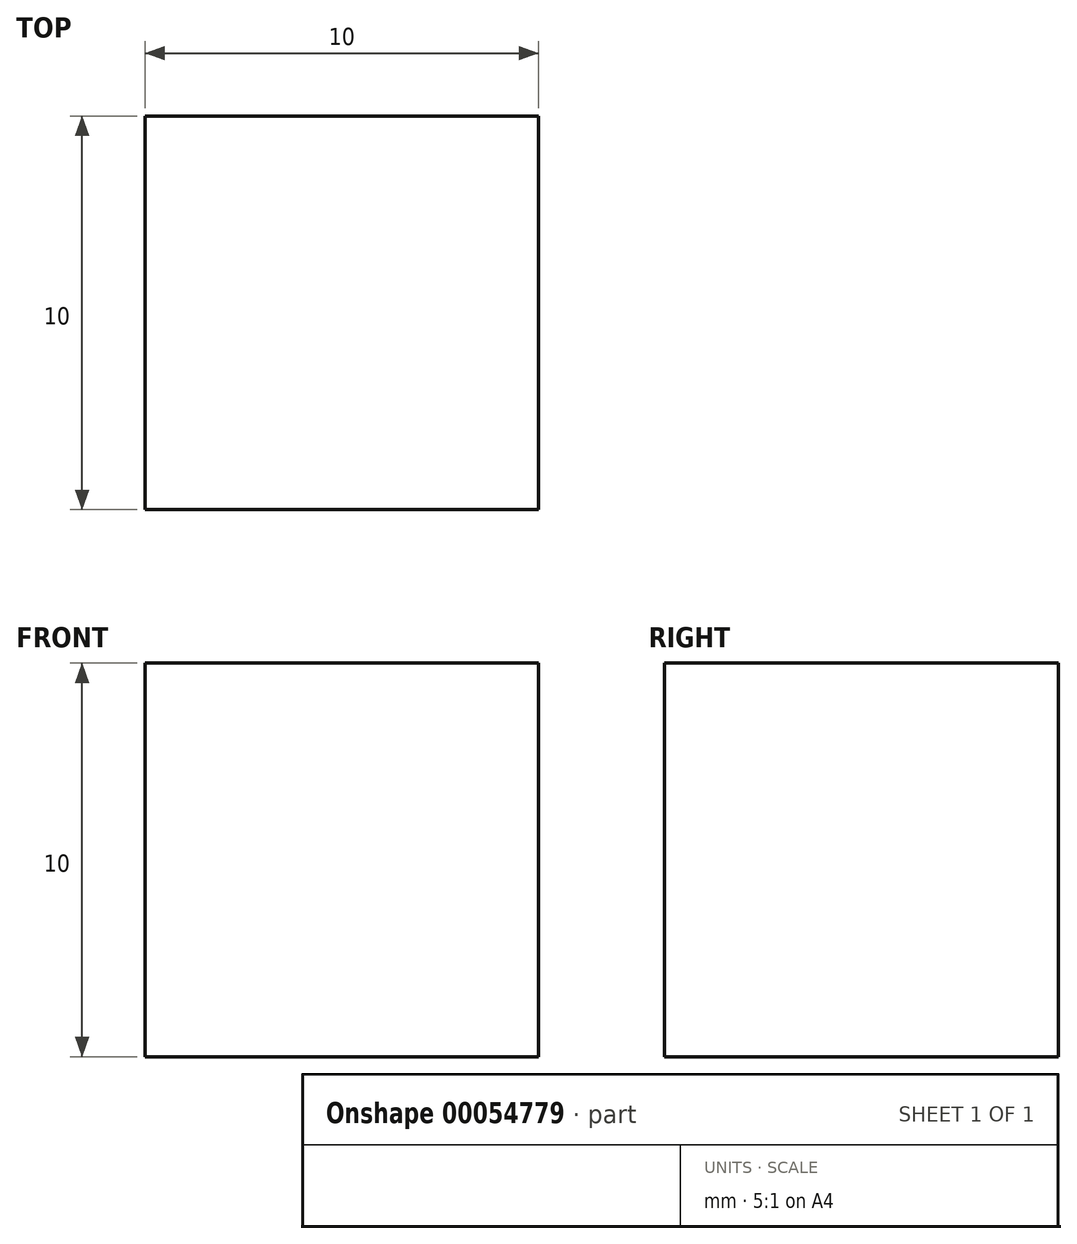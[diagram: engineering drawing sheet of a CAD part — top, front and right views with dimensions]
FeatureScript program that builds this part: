
annotation { "Feature Type Name" : "Feature", "Feature Type Description" : "" }
export const myFeature = defineFeature(function(context is Context, id is Id, definition is map)
    precondition{}
    {
        {
            var Q0;
            Q0=qCreatedBy(makeId("Top.planeOp"),FACE);
            var sketch = newSketch(context, id + "F0", { "sketchPlane" : qUnion([Q0])});
            skLineSegment(sketch, "E0.bottom", {"start": v(0, 0) * mm, "end": v(10, 0) * mm});
            skLineSegment(sketch, "E0.top", {"start": v(0, 10) * mm, "end": v(10, 10) * mm});
            skLineSegment(sketch, "E0.left", {"start": v(0, 0) * mm, "end": v(0, 10) * mm});
            skLineSegment(sketch, "E0.right", {"start": v(10, 0) * mm, "end": v(10, 10) * mm});
            skSolve(sketch);
        }
        {
            var Q0;
            Q0=makeQuery(id+"F0.imprint","IMPRINT",FACE,{"disambiguationData":[TD([[makeQuery(id+"F0.imprint","IMPRINT",EDGE,{"derivedFrom":sQuery(id+"F0.wireOp",EDGE,"E0.bottom")}),1.0]])]});
            extrude(context, id + "F1", {"entities" : qUnion([Q0]), "depth" : 10 * mm});
        }
    });
